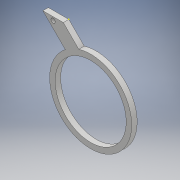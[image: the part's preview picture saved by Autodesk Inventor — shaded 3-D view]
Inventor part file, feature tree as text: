
AUTODESK INVENTOR PART (.ipt)
format: ipt  version: 2017 (Build 210142000, 142)  size: 119,808 bytes
history: native  units: mm
features: sketch x2, extrude x1
ambient origin geometry x8: Origin, YZ Plane, XZ Plane, XY Plane, X Axis, Y Axis, Z Axis, Center Point
bodies: Solid1 (feature_tree)
feature tree (3):
  extrude  "Extrusion1"  Depth=15.0mm
  sketch  "Sketch2"  dims[d2=7.5mm d3=3.2mm d4=135.0deg d6=52.0mm d7=40.0mm d8=60.0mm d10=20.0mm d11=135.0deg d12=4.0mm d13=0.0mm]
  sketch  "Sketch1"  dims[d0=15.0mm d1=2.5mm]
